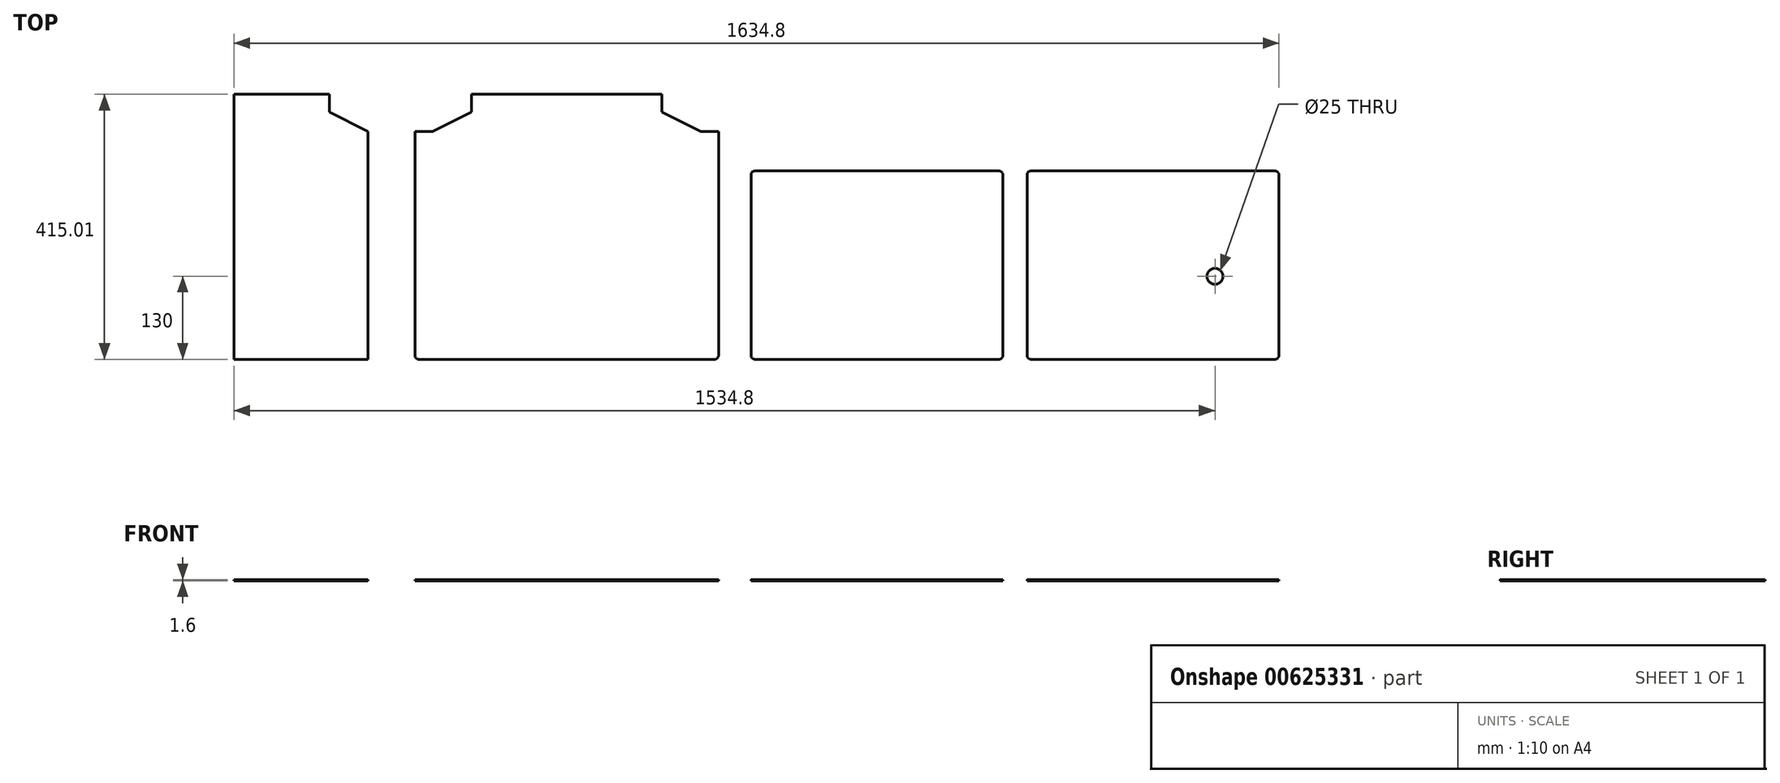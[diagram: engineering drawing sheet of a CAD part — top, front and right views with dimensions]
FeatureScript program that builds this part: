
annotation { "Feature Type Name" : "Feature", "Feature Type Description" : "" }
export const myFeature = defineFeature(function(context is Context, id is Id, definition is map)
    precondition{}
    {
        {
            var Q0;
            Q0=qCreatedBy(makeId("Top.planeOp"),FACE);
            var sketch = newSketch(context, id + "F0", { "sketchPlane" : qUnion([Q0])});
            skLineSegment(sketch, "E0.bottom", {"start": v(413.05, 295) * mm, "end": v(31.75, 295) * mm});
            skLineSegment(sketch, "E0.top", {"start": v(413.05, 0) * mm, "end": v(31.75, 0) * mm});
            skLineSegment(sketch, "E0.left", {"start": v(419.4, 288.65) * mm, "end": v(419.4, 6.35) * mm});
            skLineSegment(sketch, "E0.right", {"start": v(25.4, 288.65) * mm, "end": v(25.4, 6.35) * mm});
            skLineSegment(sketch, "E1.bottom", {"start": v(463.55, 0) * mm, "end": v(844.85, 0) * mm});
            skLineSegment(sketch, "E1.top", {"start": v(463.55, 295) * mm, "end": v(844.85, 295) * mm});
            skLineSegment(sketch, "E1.left", {"start": v(457.2, 6.35) * mm, "end": v(457.2, 288.65) * mm});
            skLineSegment(sketch, "E1.right", {"start": v(851.2, 6.35) * mm, "end": v(851.2, 288.65) * mm});
            skPoint(sketch, "E2.visualSharp", {"position": v(25.4, 295) * mm});
            skArc(sketch, "E2.filletArc", {"start": v(31.75, 295) * mm, "mid": v(27.26, 293.14) * mm, "end": v(25.4, 288.65) * mm});
            skPoint(sketch, "E3.visualSharp", {"position": v(419.4, 295) * mm});
            skArc(sketch, "E3.filletArc", {"start": v(419.4, 288.65) * mm, "mid": v(417.54, 293.14) * mm, "end": v(413.05, 295) * mm});
            skPoint(sketch, "E4.visualSharp", {"position": v(419.4, 0) * mm});
            skArc(sketch, "E4.filletArc", {"start": v(413.05, 0) * mm, "mid": v(417.54, 1.86) * mm, "end": v(419.4, 6.35) * mm});
            skPoint(sketch, "E5.visualSharp", {"position": v(25.4, 0) * mm});
            skArc(sketch, "E5.filletArc", {"start": v(25.4, 6.35) * mm, "mid": v(27.26, 1.86) * mm, "end": v(31.75, 0) * mm});
            skPoint(sketch, "E6.visualSharp", {"position": v(457.2, 0) * mm});
            skArc(sketch, "E6.filletArc", {"start": v(457.2, 6.35) * mm, "mid": v(459.06, 1.86) * mm, "end": v(463.55, 0) * mm});
            skPoint(sketch, "E7.visualSharp", {"position": v(457.2, 295) * mm});
            skArc(sketch, "E7.filletArc", {"start": v(463.55, 295) * mm, "mid": v(459.06, 293.14) * mm, "end": v(457.2, 288.65) * mm});
            skPoint(sketch, "E8.visualSharp", {"position": v(851.2, 295) * mm});
            skArc(sketch, "E8.filletArc", {"start": v(851.2, 288.65) * mm, "mid": v(849.34, 293.14) * mm, "end": v(844.85, 295) * mm});
            skPoint(sketch, "E9.visualSharp", {"position": v(851.2, 0) * mm});
            skArc(sketch, "E9.filletArc", {"start": v(844.85, 0) * mm, "mid": v(849.34, 1.86) * mm, "end": v(851.2, 6.35) * mm});
            skLineSegment(sketch, "E10", {"start": v(457.2, 0) * mm, "end": v(851.2, 0) * mm, "construction": true});
            skLineSegment(sketch, "E11", {"start": v(419.4, 0) * mm, "end": v(25.4, 0) * mm, "construction": true});
            skCircle(sketch, "E12", {"center": v(751.2, 130) * mm, "radius": 12.5 * mm});
            skLineSegment(sketch, "E13.bottom", {"start": v(-31.75, 0) * mm, "end": v(-494.05, 0) * mm});
            skLineSegment(sketch, "E13.top", {"start": v(-31.75, 415) * mm, "end": v(-494.05, 415) * mm});
            skLineSegment(sketch, "E13.left", {"start": v(-25.4, 6.35) * mm, "end": v(-25.4, 408.65) * mm});
            skLineSegment(sketch, "E13.right", {"start": v(-500.4, 6.35) * mm, "end": v(-500.4, 408.65) * mm});
            skPoint(sketch, "E14.visualSharp", {"position": v(-500.4, 415) * mm});
            skArc(sketch, "E14.filletArc", {"start": v(-494.05, 415) * mm, "mid": v(-498.54, 413.14) * mm, "end": v(-500.4, 408.65) * mm});
            skPoint(sketch, "E15.visualSharp", {"position": v(-25.4, 415) * mm});
            skArc(sketch, "E15.filletArc", {"start": v(-25.4, 408.65) * mm, "mid": v(-27.26, 413.14) * mm, "end": v(-31.75, 415) * mm});
            skPoint(sketch, "E16.visualSharp", {"position": v(-25.4, 0) * mm});
            skArc(sketch, "E16.filletArc", {"start": v(-31.75, 0) * mm, "mid": v(-27.26, 1.86) * mm, "end": v(-25.4, 6.35) * mm});
            skPoint(sketch, "E17.visualSharp", {"position": v(-500.4, 0) * mm});
            skArc(sketch, "E17.filletArc", {"start": v(-500.4, 6.35) * mm, "mid": v(-498.54, 1.86) * mm, "end": v(-494.05, 0) * mm});
            skLineSegment(sketch, "E18.bottom", {"start": v(-500.4, 415) * mm, "end": v(-412.12, 415) * mm});
            skLineSegment(sketch, "E18.top", {"start": v(-500.4, 387.06) * mm, "end": v(-412.12, 387.06) * mm});
            skLineSegment(sketch, "E18.left", {"start": v(-500.4, 415) * mm, "end": v(-500.4, 387.06) * mm});
            skLineSegment(sketch, "E18.right", {"start": v(-412.12, 415) * mm, "end": v(-412.12, 387.06) * mm});
            skLineSegment(sketch, "E19.bottom", {"start": v(-25.4, 415) * mm, "end": v(-113.67, 415) * mm});
            skLineSegment(sketch, "E19.top", {"start": v(-25.4, 387.06) * mm, "end": v(-113.67, 387.06) * mm});
            skLineSegment(sketch, "E19.left", {"start": v(-25.4, 415) * mm, "end": v(-25.4, 387.06) * mm});
            skLineSegment(sketch, "E19.right", {"start": v(-113.67, 415) * mm, "end": v(-113.67, 387.06) * mm});
            skLineSegment(sketch, "E20.bottom", {"start": v(-500.4, 387.06) * mm, "end": v(-472.46, 387.06) * mm});
            skLineSegment(sketch, "E20.top", {"start": v(-500.4, 356.58) * mm, "end": v(-472.46, 356.58) * mm});
            skLineSegment(sketch, "E20.left", {"start": v(-500.4, 387.06) * mm, "end": v(-500.4, 356.58) * mm});
            skLineSegment(sketch, "E20.right", {"start": v(-472.46, 387.06) * mm, "end": v(-472.46, 356.58) * mm});
            skLineSegment(sketch, "E21.bottom", {"start": v(-25.4, 387.06) * mm, "end": v(-53.34, 387.06) * mm});
            skLineSegment(sketch, "E21.top", {"start": v(-25.4, 356.58) * mm, "end": v(-53.34, 356.58) * mm});
            skLineSegment(sketch, "E21.left", {"start": v(-25.4, 387.06) * mm, "end": v(-25.4, 356.58) * mm});
            skLineSegment(sketch, "E21.right", {"start": v(-53.34, 387.06) * mm, "end": v(-53.34, 356.58) * mm});
            skLineSegment(sketch, "E22", {"start": v(-472.46, 356.58) * mm, "end": v(-412.12, 387.06) * mm});
            skLineSegment(sketch, "E23", {"start": v(-113.67, 387.06) * mm, "end": v(-53.34, 356.58) * mm});
            skLineSegment(sketch, "E24.bottom", {"start": v(-546.1, 0) * mm, "end": v(-1021.1, 0) * mm});
            skLineSegment(sketch, "E24.top", {"start": v(-546.1, 415.01) * mm, "end": v(-1021.1, 415.01) * mm});
            skLineSegment(sketch, "E24.left", {"start": v(-546.1, 0) * mm, "end": v(-546.1, 415.01) * mm});
            skLineSegment(sketch, "E24.right", {"start": v(-1021.1, 0) * mm, "end": v(-1021.1, 415.01) * mm});
            skLineSegment(sketch, "E25", {"start": v(-783.6, 415.01) * mm, "end": v(-783.6, 0) * mm});
            skLineSegment(sketch, "E26.bottom", {"start": v(-546.1, 415.01) * mm, "end": v(-634.38, 415.01) * mm});
            skLineSegment(sketch, "E26.top", {"start": v(-546.1, 387.07) * mm, "end": v(-634.38, 387.07) * mm});
            skLineSegment(sketch, "E26.left", {"start": v(-546.1, 415.01) * mm, "end": v(-546.1, 387.07) * mm});
            skLineSegment(sketch, "E26.right", {"start": v(-634.38, 415.01) * mm, "end": v(-634.38, 387.07) * mm});
            skLineSegment(sketch, "E27.bottom", {"start": v(-546.1, 387.07) * mm, "end": v(-574.04, 387.07) * mm});
            skLineSegment(sketch, "E27.top", {"start": v(-546.1, 356.6) * mm, "end": v(-574.04, 356.6) * mm});
            skLineSegment(sketch, "E27.left", {"start": v(-546.1, 387.07) * mm, "end": v(-546.1, 356.6) * mm});
            skLineSegment(sketch, "E27.right", {"start": v(-574.04, 387.07) * mm, "end": v(-574.04, 356.6) * mm});
            skLineSegment(sketch, "E28.bottom", {"start": v(-1021.1, 415.01) * mm, "end": v(-932.83, 415.01) * mm});
            skLineSegment(sketch, "E28.top", {"start": v(-1021.1, 387.07) * mm, "end": v(-932.83, 387.07) * mm});
            skLineSegment(sketch, "E28.left", {"start": v(-1021.1, 415.01) * mm, "end": v(-1021.1, 387.07) * mm});
            skLineSegment(sketch, "E28.right", {"start": v(-932.83, 415.01) * mm, "end": v(-932.83, 387.07) * mm});
            skLineSegment(sketch, "E29.bottom", {"start": v(-1021.1, 387.07) * mm, "end": v(-993.17, 387.07) * mm});
            skLineSegment(sketch, "E29.top", {"start": v(-1021.1, 356.6) * mm, "end": v(-993.17, 356.6) * mm});
            skLineSegment(sketch, "E29.left", {"start": v(-1021.1, 387.07) * mm, "end": v(-1021.1, 356.6) * mm});
            skLineSegment(sketch, "E29.right", {"start": v(-993.17, 387.07) * mm, "end": v(-993.17, 356.6) * mm});
            skLineSegment(sketch, "E30", {"start": v(-993.17, 356.6) * mm, "end": v(-932.83, 387.07) * mm});
            skLineSegment(sketch, "E31", {"start": v(-634.38, 387.07) * mm, "end": v(-574.04, 356.6) * mm});
            skLineSegment(sketch, "E32.bottom", {"start": v(-574.04, 356.6) * mm, "end": v(-546.1, 356.6) * mm});
            skLineSegment(sketch, "E32.top", {"start": v(-574.04, 0) * mm, "end": v(-546.1, 0) * mm});
            skLineSegment(sketch, "E32.left", {"start": v(-574.04, 356.6) * mm, "end": v(-574.04, 0) * mm});
            skLineSegment(sketch, "E32.right", {"start": v(-546.1, 356.6) * mm, "end": v(-546.1, 0) * mm});
            skSolve(sketch);
        }
        {
            var Q0;
            Q0=makeQuery(id+"F0.imprint","IMPRINT",FACE,{"disambiguationData":[TD([[makeQuery(id+"F0.imprint","IMPRINT",EDGE,{"derivedFrom":sQuery(id+"F0.wireOp",EDGE,"E0.bottom")}),1.0]])]});
            var Q1;
            Q1=makeQuery(id+"F0.imprint","IMPRINT",FACE,{"disambiguationData":[TD([[makeQuery(id+"F0.imprint","IMPRINT",EDGE,{"derivedFrom":sQuery(id+"F0.wireOp",EDGE,"E1.bottom")}),1.0]])]});
            var Q2;
            Q2=makeQuery(id+"F0.imprint","IMPRINT",FACE,{"disambiguationData":[TD([[makeQuery(id+"F0.imprint","IMPRINT",EDGE,{"derivedFrom":sQuery(id+"F0.wireOp",EDGE,"E13.bottom")}),-1.0]])]});
            var Q3;
            {var subQ2=sQuery(id+"F0.wireOp",EDGE,"E25");Q3=makeQuery(id+"F0.imprint","IMPRINT",FACE,{"disambiguationData":[TD([[makeQuery(id+"F0.imprint","IMPRINT",EDGE,{"derivedFrom":subQ2}),1.0]])]});}
            extrude(context, id + "F1", {"entities" : qUnion([Q0, Q1, Q2, Q3]), "depth" : 1.6 * mm, "offsetDistance" : 25.4 * mm});
        }
    });
